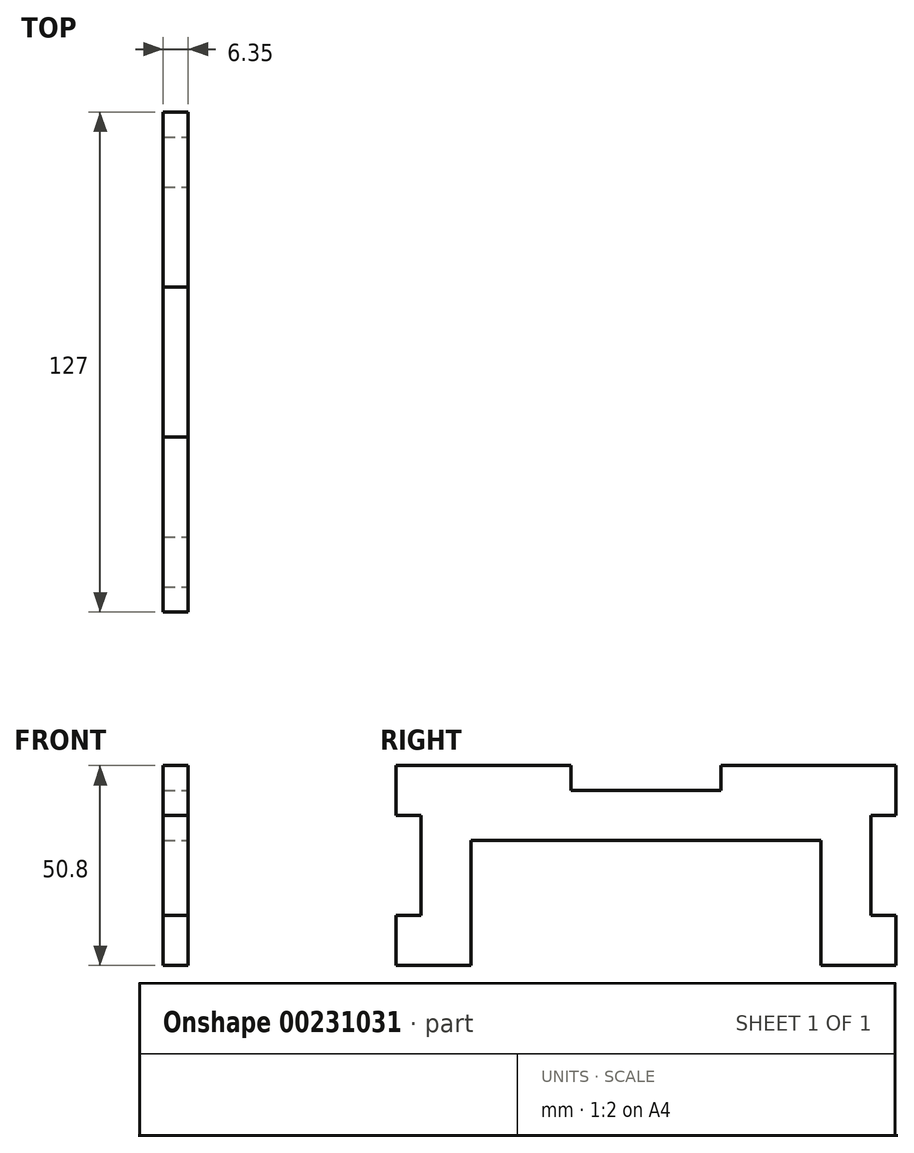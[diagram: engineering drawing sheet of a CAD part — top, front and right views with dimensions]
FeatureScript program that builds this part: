
annotation { "Feature Type Name" : "Feature", "Feature Type Description" : "" }
export const myFeature = defineFeature(function(context is Context, id is Id, definition is map)
    precondition{}
    {
        {
            var Q0;
            Q0=qCreatedBy(makeId("Right.planeOp"),FACE);
            var sketch = newSketch(context, id + "F0", { "sketchPlane" : qUnion([Q0])});
            skLineSegment(sketch, "E0.top", {"start": v(57.15, 25.4) * mm, "end": v(50.8, 25.4) * mm});
            skLineSegment(sketch, "E0.left", {"start": v(63.5, -19.05) * mm, "end": v(63.5, -12.7) * mm});
            skLineSegment(sketch, "E0.right", {"start": v(-63.5, -19.05) * mm, "end": v(-63.5, -12.7) * mm});
            skPoint(sketch, "E0.middle", {"position": v(0, 0) * mm});
            skLineSegment(sketch, "E1.left", {"start": v(44.45, -25.4) * mm, "end": v(44.45, 6.35) * mm});
            skLineSegment(sketch, "E1.right", {"start": v(-44.45, -25.4) * mm, "end": v(-44.45, 6.35) * mm});
            skLineSegment(sketch, "E2", {"start": v(-44.45, 6.35) * mm, "end": v(44.45, 6.35) * mm});
            skLineSegment(sketch, "E3.trimOffspring", {"start": v(-44.45, -25.4) * mm, "end": v(-50.8, -25.4) * mm});
            skLineSegment(sketch, "E4", {"start": v(-63.5, 12.7) * mm, "end": v(-57.15, 12.7) * mm});
            skLineSegment(sketch, "E5.trimOffspring", {"start": v(-44.45, 6.35) * mm, "end": v(-44.45, -25.4) * mm});
            skLineSegment(sketch, "E6.MirrorCS", {"start": v(-19.05, 25.4) * mm, "end": v(-19.05, 19.05) * mm});
            skLineSegment(sketch, "E7.MirrorCS", {"start": v(-63.5, -12.7) * mm, "end": v(-57.15, -12.7) * mm});
            skLineSegment(sketch, "E8.MirrorCS", {"start": v(63.5, 12.7) * mm, "end": v(57.15, 12.7) * mm});
            skLineSegment(sketch, "E9.MirrorCS", {"start": v(63.5, -12.7) * mm, "end": v(57.15, -12.7) * mm});
            skLineSegment(sketch, "E10.trimOffspring", {"start": v(50.8, -25.4) * mm, "end": v(44.45, -25.4) * mm});
            skLineSegment(sketch, "E11.trimOffspring", {"start": v(44.45, 25.4) * mm, "end": v(38.1, 25.4) * mm});
            skLineSegment(sketch, "E12.trimOffspring", {"start": v(31.75, 25.4) * mm, "end": v(25.4, 25.4) * mm});
            skLineSegment(sketch, "E13.trimOffspring", {"start": v(-19.05, 25.4) * mm, "end": v(-25.4, 25.4) * mm});
            skLineSegment(sketch, "E14.trimOffspring", {"start": v(-31.75, 25.4) * mm, "end": v(-38.1, 25.4) * mm});
            skLineSegment(sketch, "E15.trimOffspring", {"start": v(-44.45, 25.4) * mm, "end": v(-50.8, 25.4) * mm});
            skLineSegment(sketch, "E16.trimOffspring", {"start": v(57.15, -6.35) * mm, "end": v(57.15, -12.7) * mm});
            skLineSegment(sketch, "E17.trimOffspring", {"start": v(57.15, 6.35) * mm, "end": v(57.15, 0) * mm});
            skLineSegment(sketch, "E18.trimOffspring", {"start": v(6.35, 19.05) * mm, "end": v(12.7, 19.05) * mm});
            skLineSegment(sketch, "E19.trimOffspring", {"start": v(-6.35, 19.05) * mm, "end": v(0, 19.05) * mm});
            skLineSegment(sketch, "E20.trimOffspring", {"start": v(-19.05, 19.05) * mm, "end": v(-12.7, 19.05) * mm});
            skLineSegment(sketch, "E21.trimOffspring", {"start": v(-57.15, 6.35) * mm, "end": v(-57.15, 0) * mm});
            skLineSegment(sketch, "E22.trimOffspring", {"start": v(-57.15, -6.35) * mm, "end": v(-57.15, -12.7) * mm});
            skLineSegment(sketch, "E23", {"start": v(-63.5, 12.7) * mm, "end": v(-63.5, 25.4) * mm});
            skLineSegment(sketch, "E24", {"start": v(-63.5, 25.4) * mm, "end": v(-50.8, 25.4) * mm});
            skLineSegment(sketch, "E25", {"start": v(-63.5, -19.05) * mm, "end": v(-63.5, -25.4) * mm});
            skLineSegment(sketch, "E26", {"start": v(-63.5, -25.4) * mm, "end": v(-50.8, -25.4) * mm});
            skLineSegment(sketch, "E27", {"start": v(-57.15, 12.7) * mm, "end": v(-57.15, 6.35) * mm});
            skLineSegment(sketch, "E28", {"start": v(-57.15, 0) * mm, "end": v(-57.15, -6.35) * mm});
            skLineSegment(sketch, "E29", {"start": v(-44.45, 25.4) * mm, "end": v(-38.1, 25.4) * mm});
            skLineSegment(sketch, "E30", {"start": v(-31.75, 25.4) * mm, "end": v(-25.4, 25.4) * mm});
            skLineSegment(sketch, "E31", {"start": v(57.15, 25.4) * mm, "end": v(63.5, 25.4) * mm});
            skLineSegment(sketch, "E32", {"start": v(63.5, 25.4) * mm, "end": v(63.5, 12.7) * mm});
            skLineSegment(sketch, "E33", {"start": v(57.15, 12.7) * mm, "end": v(57.15, 6.35) * mm});
            skLineSegment(sketch, "E34", {"start": v(57.15, 0) * mm, "end": v(57.15, -6.35) * mm});
            skLineSegment(sketch, "E35", {"start": v(50.8, -25.4) * mm, "end": v(63.5, -25.4) * mm});
            skLineSegment(sketch, "E36", {"start": v(63.5, -25.4) * mm, "end": v(63.5, -19.05) * mm});
            skLineSegment(sketch, "E37", {"start": v(50.8, 25.4) * mm, "end": v(44.45, 25.4) * mm});
            skLineSegment(sketch, "E38", {"start": v(38.1, 25.4) * mm, "end": v(31.75, 25.4) * mm});
            skLineSegment(sketch, "E39", {"start": v(25.4, 25.4) * mm, "end": v(19.05, 25.4) * mm});
            skLineSegment(sketch, "E40", {"start": v(-12.7, 19.05) * mm, "end": v(-6.35, 19.05) * mm});
            skLineSegment(sketch, "E41", {"start": v(0, 19.05) * mm, "end": v(6.35, 19.05) * mm});
            skLineSegment(sketch, "E42", {"start": v(19.05, 25.4) * mm, "end": v(19.05, 19.05) * mm});
            skLineSegment(sketch, "E43", {"start": v(19.05, 19.05) * mm, "end": v(12.7, 19.05) * mm});
            skSolve(sketch);
        }
        {
            var Q0;
            {var subQ5=sQuery(id+"F0.wireOp",EDGE,"E0.top");Q0=makeQuery(id+"F0.imprint","IMPRINT",FACE,{"disambiguationData":[TD([[makeQuery(id+"F0.imprint","IMPRINT",EDGE,{"derivedFrom":subQ5}),1.0]])]});}
            extrude(context, id + "F1", {"entities" : qUnion([Q0]), "oppositeDirection" : true, "depth" : 6.35 * mm});
        }
    });
